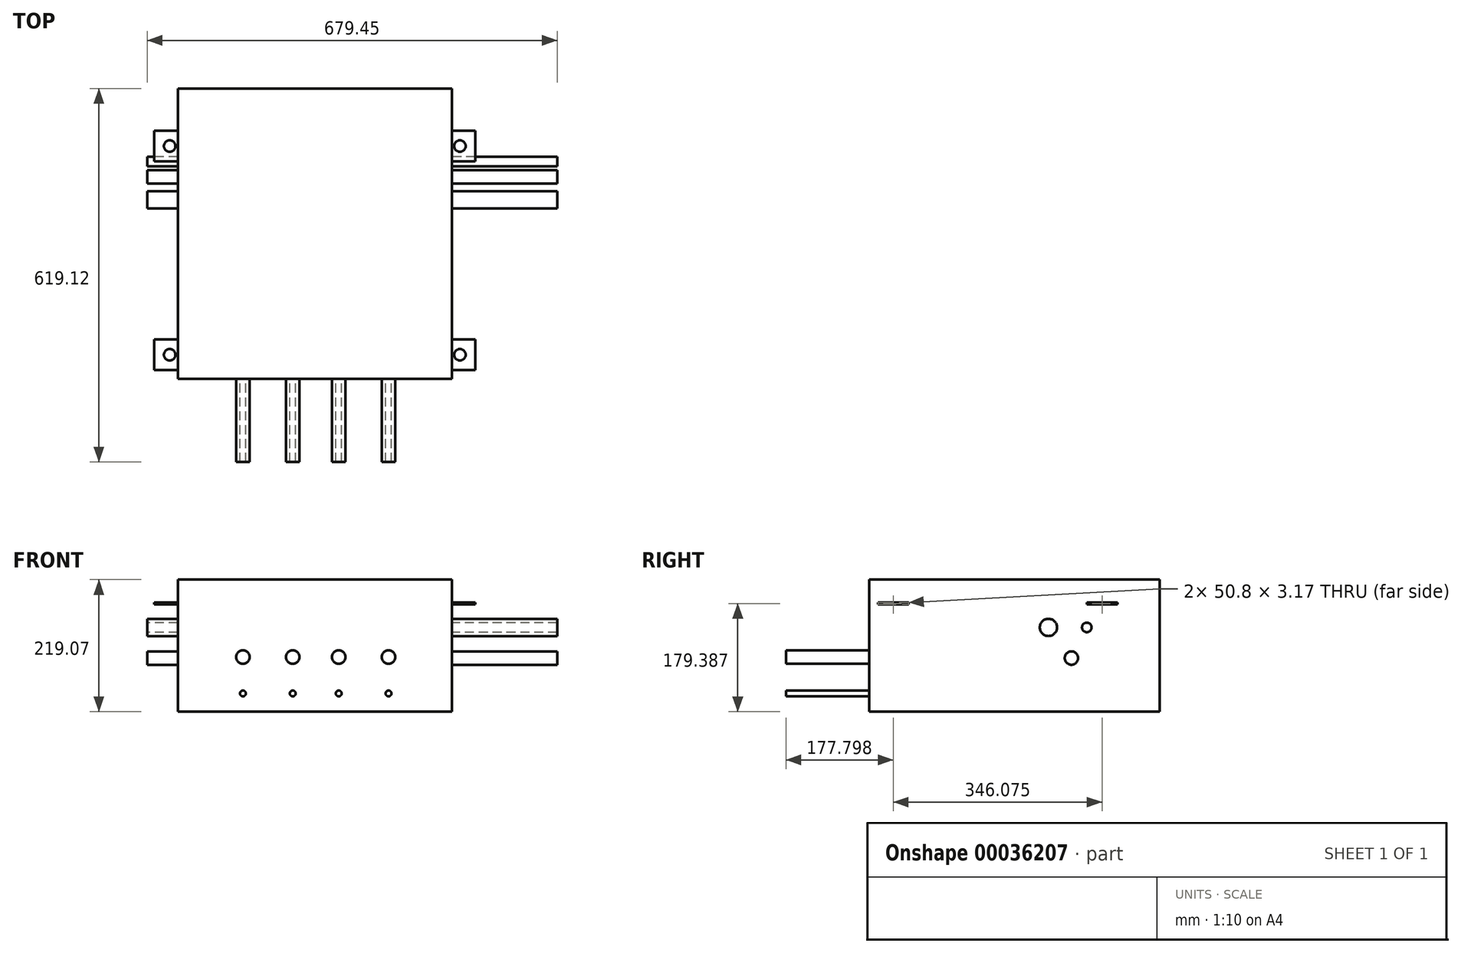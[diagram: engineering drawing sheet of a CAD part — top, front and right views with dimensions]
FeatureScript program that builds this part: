
annotation { "Feature Type Name" : "Feature", "Feature Type Description" : "" }
export const myFeature = defineFeature(function(context is Context, id is Id, definition is map)
    precondition{}
    {
        {
            var Q0;
            Q0=qCreatedBy(makeId("Front.planeOp"),FACE);
            var sketch = newSketch(context, id + "F0", { "sketchPlane" : qUnion([Q0])});
            skLineSegment(sketch, "E0.bottom", {"start": v(0, 0) * mm, "end": v(454.03, 0) * mm});
            skLineSegment(sketch, "E0.top", {"start": v(0, 219.07) * mm, "end": v(454.03, 219.07) * mm});
            skLineSegment(sketch, "E0.left", {"start": v(0, 0) * mm, "end": v(0, 219.07) * mm});
            skLineSegment(sketch, "E0.right", {"start": v(454.03, 0) * mm, "end": v(454.03, 219.08) * mm});
            skSolve(sketch);
        }
        {
            var Q0;
            Q0=qSketchRegion(id+"F0",true);
            extrude(context, id + "F1", {"entities" : qUnion([Q0]), "oppositeDirection" : true, "depth" : 481 * mm});
        }
        {
            var Q0;
            Q0=qCreatedBy(makeId("Front.planeOp"),FACE);
            var sketch = newSketch(context, id + "F2", { "sketchPlane" : qUnion([Q0])});
            skLineSegment(sketch, "E1.bottom", {"start": v(107.95, 90.49) * mm, "end": v(349.25, 90.49) * mm, "construction": true});
            skLineSegment(sketch, "E1.top", {"start": v(107.95, 30.16) * mm, "end": v(349.25, 30.16) * mm, "construction": true});
            skLineSegment(sketch, "E1.left", {"start": v(107.95, 90.49) * mm, "end": v(107.95, 30.16) * mm, "construction": true});
            skLineSegment(sketch, "E1.right", {"start": v(349.25, 90.49) * mm, "end": v(349.25, 30.16) * mm, "construction": true});
            skCircle(sketch, "E2", {"center": v(107.95, 90.49) * mm, "radius": 11.11 * mm});
            skCircle(sketch, "E3", {"center": v(107.95, 30.16) * mm, "radius": 4.76 * mm});
            skCircle(sketch, "E4", {"center": v(349.25, 90.49) * mm, "radius": 11.11 * mm});
            skCircle(sketch, "E5", {"center": v(349.25, 30.16) * mm, "radius": 4.76 * mm});
            skCircle(sketch, "E6", {"center": v(190.5, 90.49) * mm, "radius": 11.11 * mm});
            skCircle(sketch, "E7", {"center": v(266.7, 90.49) * mm, "radius": 11.11 * mm});
            skCircle(sketch, "E8", {"center": v(190.5, 30.16) * mm, "radius": 4.76 * mm});
            skCircle(sketch, "E9", {"center": v(266.7, 30.16) * mm, "radius": 4.76 * mm});
            skLineSegment(sketch, "E10", {"start": v(190.5, 30.16) * mm, "end": v(190.5, 90.49) * mm, "construction": true});
            skLineSegment(sketch, "E11", {"start": v(266.7, 30.16) * mm, "end": v(266.7, 90.49) * mm, "construction": true});
            skSolve(sketch);
        }
        {
            var Q0;
            Q0=qSketchRegion(id+"F2",true);
            extrude(context, id + "F3", {"entities" : qUnion([Q0]), "operationType" : NewBodyOperationType.ADD, "depth" : 138.11 * mm});
        }
        {
            var Q0;
            Q0=makeQuery(id+"F1.opExtrude","SWEPT_FACE",FACE,{"disambiguationData":[OSD([sQuery(id+"F0.wireOp",EDGE,"E0.right")])]});
            var sketch = newSketch(context, id + "F4", { "sketchPlane" : qUnion([Q0])});
            skCircle(sketch, "E12", {"center": v(296.86, 139.7) * mm, "radius": 14.29 * mm});
            skCircle(sketch, "E13", {"center": v(360.36, 139.7) * mm, "radius": 7.94 * mm});
            skCircle(sketch, "E14", {"center": v(334.96, 88.9) * mm, "radius": 11.11 * mm});
            skSolve(sketch);
        }
        {
            var Q0;
            Q0=qSketchRegion(id+"F4",true);
            extrude(context, id + "F5", {"entities" : qUnion([Q0]), "operationType" : NewBodyOperationType.ADD, "depth" : 174.62 * mm, "hasSecondDirection" : true, "secondDirectionOppositeDirection" : true, "secondDirectionDepth" : 628.65 * mm});
        }
        {
            var Q0;
            Q0=makeQuery(id+"F1.opExtrude","SWEPT_FACE",FACE,{"disambiguationData":[OSD([sQuery(id+"F0.wireOp",EDGE,"E0.top")])]});
            cPlane(context, id + "F6", {"entities" : qUnion([Q0]), "cplaneType" : CPlaneType.OFFSET, "offset" : 38.1 * mm, "oppositeDirection" : true, "width" : 152.4 * mm, "height" : 152.4 * mm});
        }
        {
            var Q0;
            Q0=qCreatedBy(id+"F6.planeOp",FACE);
            var sketch = newSketch(context, id + "F7", { "sketchPlane" : qUnion([Q0])});
            skLineSegment(sketch, "E15.bottom", {"start": v(-38.9, 411.16) * mm, "end": v(0, 411.16) * mm});
            skLineSegment(sketch, "E15.top", {"start": v(-38.9, 360.36) * mm, "end": v(0, 360.36) * mm});
            skLineSegment(sketch, "E15.left", {"start": v(-38.9, 411.16) * mm, "end": v(-38.9, 360.36) * mm});
            skLineSegment(sketch, "E15.right", {"start": v(0, 411.16) * mm, "end": v(0, 360.36) * mm});
            skLineSegment(sketch, "E16.bottom", {"start": v(-38.9, 65.09) * mm, "end": v(0, 65.09) * mm});
            skLineSegment(sketch, "E16.top", {"start": v(-38.9, 14.29) * mm, "end": v(0, 14.29) * mm});
            skLineSegment(sketch, "E16.left", {"start": v(-38.9, 65.09) * mm, "end": v(-38.9, 14.29) * mm});
            skLineSegment(sketch, "E16.right", {"start": v(0, 65.09) * mm, "end": v(0, 14.29) * mm});
            skLineSegment(sketch, "E17.bottom", {"start": v(454.03, 411.16) * mm, "end": v(492.92, 411.16) * mm});
            skLineSegment(sketch, "E17.top", {"start": v(454.03, 360.36) * mm, "end": v(492.92, 360.36) * mm});
            skLineSegment(sketch, "E17.left", {"start": v(454.03, 411.16) * mm, "end": v(454.03, 360.36) * mm});
            skLineSegment(sketch, "E17.right", {"start": v(492.92, 411.16) * mm, "end": v(492.92, 360.36) * mm});
            skLineSegment(sketch, "E18.bottom", {"start": v(454.03, 65.09) * mm, "end": v(492.92, 65.09) * mm});
            skLineSegment(sketch, "E18.top", {"start": v(454.03, 14.29) * mm, "end": v(492.92, 14.29) * mm});
            skLineSegment(sketch, "E18.left", {"start": v(454.03, 65.09) * mm, "end": v(454.03, 14.29) * mm});
            skLineSegment(sketch, "E18.right", {"start": v(492.92, 65.09) * mm, "end": v(492.92, 14.29) * mm});
            skLineSegment(sketch, "E19", {"start": v(-38.9, 385.76) * mm, "end": v(-13.5, 385.76) * mm, "construction": true});
            skLineSegment(sketch, "E20", {"start": v(-38.9, 39.69) * mm, "end": v(-13.5, 39.69) * mm, "construction": true});
            skLineSegment(sketch, "E21", {"start": v(492.92, 39.69) * mm, "end": v(467.52, 39.69) * mm, "construction": true});
            skLineSegment(sketch, "E22", {"start": v(492.92, 385.76) * mm, "end": v(467.52, 385.76) * mm, "construction": true});
            skPoint(sketch, "E22.endSnap0", {"position": v(492.92, 385.76) * mm});
            skCircle(sketch, "E23", {"center": v(-13.5, 39.69) * mm, "radius": 9.53 * mm});
            skCircle(sketch, "E24", {"center": v(-13.5, 385.76) * mm, "radius": 9.53 * mm});
            skCircle(sketch, "E25", {"center": v(467.52, 385.76) * mm, "radius": 9.53 * mm});
            skCircle(sketch, "E26", {"center": v(467.52, 39.69) * mm, "radius": 9.53 * mm});
            skSolve(sketch);
        }
        {
            var Q0;
            Q0=qSketchRegion(id+"F7",true);
            extrude(context, id + "F8", {"entities" : qUnion([Q0]), "operationType" : NewBodyOperationType.ADD, "oppositeDirection" : true, "depth" : 3.17 * mm});
        }
        {
            var Q0;
            Q0=makeQuery(id+"F1.opExtrude","CAP_FACE",FACE,{"disambiguationData":[OSD([sQuery(id+"F0.wireOp",EDGE,"E0.bottom"),sQuery(id+"F0.wireOp",EDGE,"E0.top"),sQuery(id+"F0.wireOp",EDGE,"E0.left"),sQuery(id+"F0.wireOp",EDGE,"E0.right")])],"isStart":true});
            var sketch = newSketch(context, id + "F9", { "sketchPlane" : qUnion([Q0])});
            skLineSegment(sketch, "E27.bottom", {"start": v(-203.2, 219.08) * mm, "end": v(-50.8, 219.08) * mm});
            skLineSegment(sketch, "E27.top", {"start": v(-203.2, 0) * mm, "end": v(-50.8, 0) * mm});
            skLineSegment(sketch, "E27.left", {"start": v(-203.2, 219.08) * mm, "end": v(-203.2, 0) * mm});
            skLineSegment(sketch, "E27.right", {"start": v(-50.8, 219.08) * mm, "end": v(-50.8, 0) * mm});
            skSolve(sketch);
        }
        {
            var Q0;
            Q0=qSketchRegion(id+"F9",true);
            extrude(context, id + "F10", {"entities" : qUnion([Q0]), "operationType" : NewBodyOperationType.REMOVE, "endBound" : BoundingType.THROUGH_ALL, "oppositeDirection" : true, "depth" : 25.4 * mm});
        }
    });
